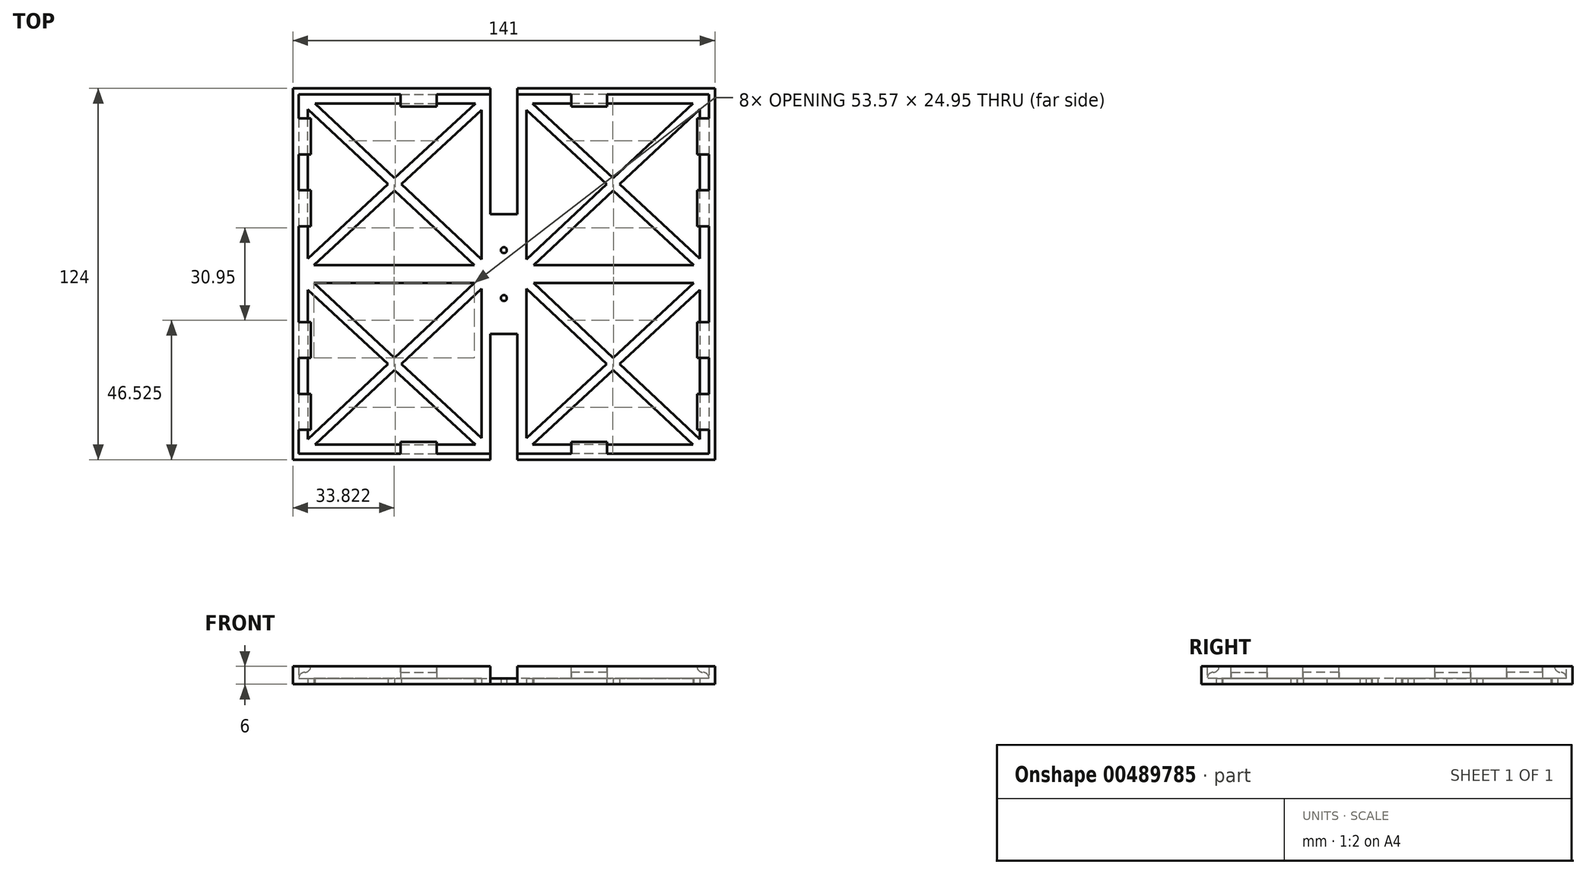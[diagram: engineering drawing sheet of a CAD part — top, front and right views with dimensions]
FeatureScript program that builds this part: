
annotation { "Feature Type Name" : "Feature", "Feature Type Description" : "" }
export const myFeature = defineFeature(function(context is Context, id is Id, definition is map)
    precondition{}
    {
        {
            var Q0;
            Q0=qCreatedBy(makeId("Top.planeOp"),FACE);
            var sketch = newSketch(context, id + "F0", { "sketchPlane" : qUnion([Q0])});
            skLineSegment(sketch, "E0.bottom", {"start": v(-68.5, 60) * mm, "end": v(-4.5, 60) * mm});
            skLineSegment(sketch, "E0.top", {"start": v(-68.5, -60) * mm, "end": v(-4.5, -60) * mm});
            skLineSegment(sketch, "E0.left", {"start": v(-68.5, 60) * mm, "end": v(-68.5, -60) * mm});
            skLineSegment(sketch, "E0.right", {"start": v(-4.5, 60) * mm, "end": v(-4.5, -60) * mm});
            skLineSegment(sketch, "E1.MirrorCS", {"start": v(68.5, 60) * mm, "end": v(4.5, 60) * mm});
            skLineSegment(sketch, "E2.MirrorCS", {"start": v(4.5, 60) * mm, "end": v(4.5, -60) * mm});
            skLineSegment(sketch, "E3.MirrorCS", {"start": v(68.5, -60) * mm, "end": v(4.5, -60) * mm});
            skLineSegment(sketch, "E4.MirrorCS", {"start": v(68.5, 60) * mm, "end": v(68.5, -60) * mm});
            skSolve(sketch);
        }
        {
            var Q0;
            Q0=qCreatedBy(makeId("Top.planeOp"),FACE);
            var sketch = newSketch(context, id + "F1", { "sketchPlane" : qUnion([Q0])});
            skLineSegment(sketch, "E5.bottom", {"start": v(-4.5, 62) * mm, "end": v(-70.5, 62) * mm});
            skLineSegment(sketch, "E5.top", {"start": v(-4.5, -62) * mm, "end": v(-70.5, -62) * mm});
            skLineSegment(sketch, "E5.left", {"start": v(-4.5, 62) * mm, "end": v(-4.5, -62) * mm});
            skLineSegment(sketch, "E5.right", {"start": v(-70.5, 62) * mm, "end": v(-70.5, -62) * mm});
            skLineSegment(sketch, "E6.bottom", {"start": v(70.5, 62) * mm, "end": v(4.5, 62) * mm});
            skLineSegment(sketch, "E6.top", {"start": v(70.5, -62) * mm, "end": v(4.5, -62) * mm});
            skLineSegment(sketch, "E6.left", {"start": v(70.5, 62) * mm, "end": v(70.5, -62) * mm});
            skLineSegment(sketch, "E6.right", {"start": v(4.5, 62) * mm, "end": v(4.5, -62) * mm});
            skLineSegment(sketch, "E7.bottom", {"start": v(-68.5, 60) * mm, "end": v(-4.5, 60) * mm});
            skLineSegment(sketch, "E7.top", {"start": v(-68.5, -60) * mm, "end": v(-4.5, -60) * mm});
            skLineSegment(sketch, "E7.left", {"start": v(-68.5, 60) * mm, "end": v(-68.5, -60) * mm});
            skLineSegment(sketch, "E7.right", {"start": v(-4.5, 60) * mm, "end": v(-4.5, -60) * mm});
            skLineSegment(sketch, "E8.bottom", {"start": v(4.5, 60) * mm, "end": v(68.5, 60) * mm});
            skLineSegment(sketch, "E8.top", {"start": v(4.5, -60) * mm, "end": v(68.5, -60) * mm});
            skLineSegment(sketch, "E8.left", {"start": v(4.5, 60) * mm, "end": v(4.5, -60) * mm});
            skLineSegment(sketch, "E8.right", {"start": v(68.5, 60) * mm, "end": v(68.5, -60) * mm});
            skSolve(sketch);
        }
        {
            var Q0;
            Q0=makeQuery(id+"F0.imprint","IMPRINT",FACE,{"disambiguationData":[TD([[makeQuery(id+"F0.imprint","IMPRINT",EDGE,{"derivedFrom":sQuery(id+"F0.wireOp",EDGE,"E0.bottom")}),-1.0]])]});
            var Q1;
            Q1=makeQuery(id+"F0.imprint","IMPRINT",FACE,{"disambiguationData":[TD([[makeQuery(id+"F0.imprint","IMPRINT",EDGE,{"derivedFrom":sQuery(id+"F0.wireOp",EDGE,"E1.MirrorCS")}),1.0]])]});
            extrude(context, id + "F2", {"entities" : qUnion([Q0, Q1]), "depth" : 2 * mm});
        }
        {
            var Q0;
            {var subQ4=sQuery(id+"F1.wireOp",EDGE,"E5.bottom");Q0=makeQuery(id+"F1.imprint","IMPRINT",FACE,{"disambiguationData":[TD([[makeQuery(id+"F1.imprint","IMPRINT",EDGE,{"derivedFrom":subQ4}),1.0]])]});}
            var Q1;
            {var subQ1=sQuery(id+"F1.wireOp",EDGE,"E6.bottom");Q1=makeQuery(id+"F1.imprint","IMPRINT",FACE,{"disambiguationData":[TD([[makeQuery(id+"F1.imprint","IMPRINT",EDGE,{"derivedFrom":subQ1}),1.0]])]});}
            extrude(context, id + "F3", {"entities" : qUnion([Q0, Q1]), "operationType" : NewBodyOperationType.ADD, "depth" : 6 * mm});
        }
        {
            var Q0;
            Q0=makeQuery(id+"F3.opExtrude","CAP_FACE",FACE,{"disambiguationData":[OSD([sQuery(id+"F1.wireOp",EDGE,"E5.bottom"),sQuery(id+"F1.wireOp",EDGE,"E5.top"),sQuery(id+"F1.wireOp",EDGE,"E5.left"),sQuery(id+"F1.wireOp",EDGE,"E5.right"),sQuery(id+"F1.wireOp",EDGE,"E7.bottom"),sQuery(id+"F1.wireOp",EDGE,"E7.top"),sQuery(id+"F1.wireOp",EDGE,"E7.left")])],"isStart":false});
            var sketch = newSketch(context, id + "F4", { "sketchPlane" : qUnion([Q0])});
            skLineSegment(sketch, "E9.bottom", {"start": v(-70.5, 52) * mm, "end": v(-64.5, 52) * mm});
            skLineSegment(sketch, "E9.top", {"start": v(-70.5, 40) * mm, "end": v(-64.5, 40) * mm});
            skLineSegment(sketch, "E9.left", {"start": v(-70.5, 52) * mm, "end": v(-70.5, 40) * mm});
            skLineSegment(sketch, "E9.right", {"start": v(-64.5, 52) * mm, "end": v(-64.5, 40) * mm});
            skLineSegment(sketch, "E10.bottom", {"start": v(-34.5, 62) * mm, "end": v(-22.5, 62) * mm});
            skLineSegment(sketch, "E10.top", {"start": v(-34.5, 56) * mm, "end": v(-22.5, 56) * mm});
            skLineSegment(sketch, "E10.left", {"start": v(-34.5, 62) * mm, "end": v(-34.5, 56) * mm});
            skLineSegment(sketch, "E10.right", {"start": v(-22.5, 62) * mm, "end": v(-22.5, 56) * mm});
            skLineSegment(sketch, "E11.bottom", {"start": v(-70.5, 16) * mm, "end": v(-64.5, 16) * mm});
            skLineSegment(sketch, "E11.top", {"start": v(-70.5, 28) * mm, "end": v(-64.5, 28) * mm});
            skLineSegment(sketch, "E11.left", {"start": v(-70.5, 16) * mm, "end": v(-70.5, 28) * mm});
            skLineSegment(sketch, "E11.right", {"start": v(-64.5, 16) * mm, "end": v(-64.5, 28) * mm});
            skLineSegment(sketch, "E12.MirrorCS", {"start": v(-22.5, -62) * mm, "end": v(-22.5, -56) * mm});
            skLineSegment(sketch, "E13.MirrorCS", {"start": v(-34.5, -62) * mm, "end": v(-34.5, -56) * mm});
            skLineSegment(sketch, "E14.MirrorCS", {"start": v(-64.5, -16) * mm, "end": v(-64.5, -28) * mm});
            skLineSegment(sketch, "E15.MirrorCS", {"start": v(-70.5, -52) * mm, "end": v(-70.5, -40) * mm});
            skLineSegment(sketch, "E16.MirrorCS", {"start": v(-70.5, -16) * mm, "end": v(-70.5, -28) * mm});
            skLineSegment(sketch, "E17.MirrorCS", {"start": v(-70.5, -28) * mm, "end": v(-64.5, -28) * mm});
            skLineSegment(sketch, "E18.MirrorCS", {"start": v(-70.5, -40) * mm, "end": v(-64.5, -40) * mm});
            skLineSegment(sketch, "E19.MirrorCS", {"start": v(-70.5, -52) * mm, "end": v(-64.5, -52) * mm});
            skLineSegment(sketch, "E20.MirrorCS", {"start": v(-70.5, -16) * mm, "end": v(-64.5, -16) * mm});
            skLineSegment(sketch, "E21.MirrorCS", {"start": v(-64.5, -52) * mm, "end": v(-64.5, -40) * mm});
            skLineSegment(sketch, "E22.MirrorCS", {"start": v(-34.5, -56) * mm, "end": v(-22.5, -56) * mm});
            skLineSegment(sketch, "E23.MirrorCS", {"start": v(-34.5, -62) * mm, "end": v(-22.5, -62) * mm});
            skLineSegment(sketch, "E24.MirrorCS", {"start": v(70.5, 40) * mm, "end": v(64.5, 40) * mm});
            skLineSegment(sketch, "E25.MirrorCS", {"start": v(70.5, -28) * mm, "end": v(64.5, -28) * mm});
            skLineSegment(sketch, "E26.MirrorCS", {"start": v(70.5, -40) * mm, "end": v(64.5, -40) * mm});
            skLineSegment(sketch, "E27.MirrorCS", {"start": v(70.5, -52) * mm, "end": v(64.5, -52) * mm});
            skLineSegment(sketch, "E28.MirrorCS", {"start": v(34.5, 62) * mm, "end": v(34.5, 56) * mm});
            skLineSegment(sketch, "E29.MirrorCS", {"start": v(22.5, 62) * mm, "end": v(22.5, 56) * mm});
            skLineSegment(sketch, "E30.MirrorCS", {"start": v(70.5, 16) * mm, "end": v(64.5, 16) * mm});
            skLineSegment(sketch, "E31.MirrorCS", {"start": v(70.5, 28) * mm, "end": v(64.5, 28) * mm});
            skLineSegment(sketch, "E32.MirrorCS", {"start": v(70.5, -16) * mm, "end": v(64.5, -16) * mm});
            skLineSegment(sketch, "E33.MirrorCS", {"start": v(70.5, 52) * mm, "end": v(64.5, 52) * mm});
            skLineSegment(sketch, "E34.MirrorCS", {"start": v(64.5, 16) * mm, "end": v(64.5, 28) * mm});
            skLineSegment(sketch, "E35.MirrorCS", {"start": v(34.5, -62) * mm, "end": v(22.5, -62) * mm});
            skLineSegment(sketch, "E36.MirrorCS", {"start": v(34.5, -56) * mm, "end": v(22.5, -56) * mm});
            skLineSegment(sketch, "E37.MirrorCS", {"start": v(70.5, 52) * mm, "end": v(70.5, 40) * mm});
            skLineSegment(sketch, "E38.MirrorCS", {"start": v(64.5, 52) * mm, "end": v(64.5, 40) * mm});
            skLineSegment(sketch, "E39.MirrorCS", {"start": v(64.5, -52) * mm, "end": v(64.5, -40) * mm});
            skLineSegment(sketch, "E40.MirrorCS", {"start": v(34.5, 62) * mm, "end": v(22.5, 62) * mm});
            skLineSegment(sketch, "E41.MirrorCS", {"start": v(34.5, 56) * mm, "end": v(22.5, 56) * mm});
            skLineSegment(sketch, "E42.MirrorCS", {"start": v(34.5, -62) * mm, "end": v(34.5, -56) * mm});
            skLineSegment(sketch, "E43.MirrorCS", {"start": v(70.5, -16) * mm, "end": v(70.5, -28) * mm});
            skLineSegment(sketch, "E44.MirrorCS", {"start": v(70.5, 16) * mm, "end": v(70.5, 28) * mm});
            skLineSegment(sketch, "E45.MirrorCS", {"start": v(70.5, -52) * mm, "end": v(70.5, -40) * mm});
            skLineSegment(sketch, "E46.MirrorCS", {"start": v(64.5, -16) * mm, "end": v(64.5, -28) * mm});
            skLineSegment(sketch, "E47.MirrorCS", {"start": v(22.5, -62) * mm, "end": v(22.5, -56) * mm});
            skSolve(sketch);
        }
        {
            var Q0;
            Q0=qSketchRegion(id+"F4",true);
            extrude(context, id + "F5", {"entities" : qUnion([Q0]), "operationType" : NewBodyOperationType.ADD, "oppositeDirection" : true, "depth" : 2 * mm});
        }
        {
            var Q0;
            Q0=makeQuery(id+"F2.opExtrude","CAP_FACE",FACE,{"disambiguationData":[OSD([sQuery(id+"F0.wireOp",EDGE,"E0.bottom"),sQuery(id+"F0.wireOp",EDGE,"E0.top"),sQuery(id+"F0.wireOp",EDGE,"E0.left"),sQuery(id+"F0.wireOp",EDGE,"E0.right")])],"isStart":true});
            var sketch = newSketch(context, id + "F6", { "sketchPlane" : qUnion([Q0])});
            skLineSegment(sketch, "E48", {"start": v(-63.1, 57) * mm, "end": v(-7.5, 57) * mm});
            skLineSegment(sketch, "E49", {"start": v(-7.5, 57) * mm, "end": v(-7.5, 4.87) * mm});
            skLineSegment(sketch, "E50", {"start": v(-7.5, 4.87) * mm, "end": v(-63.1, 57) * mm});
            skLineSegment(sketch, "E51", {"start": v(-65.5, 55.13) * mm, "end": v(-9.9, 3) * mm});
            skLineSegment(sketch, "E52", {"start": v(-9.9, 3) * mm, "end": v(-65.5, 3) * mm});
            skLineSegment(sketch, "E53", {"start": v(-65.5, 3) * mm, "end": v(-65.5, 55.13) * mm});
            skLineSegment(sketch, "E54", {"start": v(-9.54, 57) * mm, "end": v(-65.5, 5.2) * mm});
            skLineSegment(sketch, "E55", {"start": v(-65.5, 5.2) * mm, "end": v(-63.46, 3) * mm});
            skLineSegment(sketch, "E56", {"start": v(-63.46, 3) * mm, "end": v(-7.5, 54.8) * mm});
            skLineSegment(sketch, "E57", {"start": v(-7.5, 54.8) * mm, "end": v(-9.54, 57) * mm});
            skLineSegment(sketch, "E58", {"start": v(-68.5, 60) * mm, "end": v(-4.5, 0) * mm});
            skLineSegment(sketch, "E59.MirrorCS", {"start": v(-7.5, -54.8) * mm, "end": v(-9.54, -57) * mm});
            skLineSegment(sketch, "E60.MirrorCS", {"start": v(-65.5, -5.2) * mm, "end": v(-63.46, -3) * mm});
            skLineSegment(sketch, "E61.MirrorCS", {"start": v(-63.1, -57) * mm, "end": v(-7.5, -57) * mm});
            skLineSegment(sketch, "E62.MirrorCS", {"start": v(-7.5, -57) * mm, "end": v(-7.5, -4.87) * mm});
            skLineSegment(sketch, "E63.MirrorCS", {"start": v(-7.5, -4.87) * mm, "end": v(-63.1, -57) * mm});
            skLineSegment(sketch, "E64.MirrorCS", {"start": v(-65.5, -55.13) * mm, "end": v(-9.9, -3) * mm});
            skLineSegment(sketch, "E65.MirrorCS", {"start": v(-63.46, -3) * mm, "end": v(-7.5, -54.8) * mm});
            skLineSegment(sketch, "E66.MirrorCS", {"start": v(-9.9, -3) * mm, "end": v(-65.5, -3) * mm});
            skLineSegment(sketch, "E67.MirrorCS", {"start": v(-68.5, -60) * mm, "end": v(-4.5, 0) * mm});
            skLineSegment(sketch, "E68.MirrorCS", {"start": v(-9.54, -57) * mm, "end": v(-65.5, -5.2) * mm});
            skLineSegment(sketch, "E69.MirrorCS", {"start": v(-65.5, -3) * mm, "end": v(-65.5, -55.13) * mm});
            skLineSegment(sketch, "E70.MirrorCS", {"start": v(65.5, -5.2) * mm, "end": v(63.46, -3) * mm});
            skLineSegment(sketch, "E71.MirrorCS", {"start": v(7.5, 54.8) * mm, "end": v(9.54, 57) * mm});
            skLineSegment(sketch, "E72.MirrorCS", {"start": v(7.5, -54.8) * mm, "end": v(9.54, -57) * mm});
            skLineSegment(sketch, "E73.MirrorCS", {"start": v(65.5, 5.2) * mm, "end": v(63.46, 3) * mm});
            skLineSegment(sketch, "E74.MirrorCS", {"start": v(9.9, -3) * mm, "end": v(65.5, -3) * mm});
            skLineSegment(sketch, "E75.MirrorCS", {"start": v(63.46, 3) * mm, "end": v(7.5, 54.8) * mm});
            skLineSegment(sketch, "E76.MirrorCS", {"start": v(9.54, 57) * mm, "end": v(65.5, 5.2) * mm});
            skLineSegment(sketch, "E77.MirrorCS", {"start": v(9.9, 3) * mm, "end": v(65.5, 3) * mm});
            skLineSegment(sketch, "E78.MirrorCS", {"start": v(68.5, 60) * mm, "end": v(4.5, 0) * mm});
            skLineSegment(sketch, "E79.MirrorCS", {"start": v(65.5, 55.13) * mm, "end": v(9.9, 3) * mm});
            skLineSegment(sketch, "E80.MirrorCS", {"start": v(7.5, 4.87) * mm, "end": v(63.1, 57) * mm});
            skLineSegment(sketch, "E81.MirrorCS", {"start": v(65.5, 3) * mm, "end": v(65.5, 55.13) * mm});
            skLineSegment(sketch, "E82.MirrorCS", {"start": v(7.5, -4.87) * mm, "end": v(63.1, -57) * mm});
            skLineSegment(sketch, "E83.MirrorCS", {"start": v(7.5, -57) * mm, "end": v(7.5, -4.87) * mm});
            skLineSegment(sketch, "E84.MirrorCS", {"start": v(68.5, -60) * mm, "end": v(4.5, 0) * mm});
            skLineSegment(sketch, "E85.MirrorCS", {"start": v(63.1, 57) * mm, "end": v(7.5, 57) * mm});
            skLineSegment(sketch, "E86.MirrorCS", {"start": v(65.5, -55.13) * mm, "end": v(9.9, -3) * mm});
            skLineSegment(sketch, "E87.MirrorCS", {"start": v(7.5, 57) * mm, "end": v(7.5, 4.87) * mm});
            skLineSegment(sketch, "E88.MirrorCS", {"start": v(63.1, -57) * mm, "end": v(7.5, -57) * mm});
            skLineSegment(sketch, "E89.MirrorCS", {"start": v(9.54, -57) * mm, "end": v(65.5, -5.2) * mm});
            skLineSegment(sketch, "E90.MirrorCS", {"start": v(63.46, -3) * mm, "end": v(7.5, -54.8) * mm});
            skLineSegment(sketch, "E91.MirrorCS", {"start": v(65.5, -3) * mm, "end": v(65.5, -55.13) * mm});
            skSolve(sketch);
        }
        {
            var Q0;
            {var subQ0=sQuery(id+"F6.wireOp",EDGE,"E50");var subQ1=sQuery(id+"F6.wireOp",EDGE,"E48");var subQ2=makeQuery(id+"F6.imprint","INTERSECT",VERTEX,{"derivedFrom":[subQ1,subQ0]});Q0=makeQuery(id+"F6.imprint","IMPRINT",FACE,{"disambiguationData":[TD([[makeQuery(id+"F6.imprint","IMPRINT",EDGE,{"disambiguationData":[TD([[subQ2,1.0]])],"derivedFrom":subQ0}),-1.0]])]});}
            var Q1;
            {var subQ0=sQuery(id+"F6.wireOp",EDGE,"E50");var subQ1=sQuery(id+"F6.wireOp",EDGE,"E49");var subQ2=makeQuery(id+"F6.imprint","INTERSECT",VERTEX,{"derivedFrom":[subQ1,subQ0]});Q1=makeQuery(id+"F6.imprint","IMPRINT",FACE,{"disambiguationData":[TD([[makeQuery(id+"F6.imprint","IMPRINT",EDGE,{"disambiguationData":[TD([[subQ2,-1.0]])],"derivedFrom":subQ0}),-1.0]])]});}
            var Q2;
            {var subQ0=sQuery(id+"F6.wireOp",EDGE,"E52");var subQ1=sQuery(id+"F6.wireOp",EDGE,"E51");var subQ2=makeQuery(id+"F6.imprint","INTERSECT",VERTEX,{"derivedFrom":[subQ1,subQ0]});Q2=makeQuery(id+"F6.imprint","IMPRINT",FACE,{"disambiguationData":[TD([[makeQuery(id+"F6.imprint","IMPRINT",EDGE,{"disambiguationData":[TD([[subQ2,1.0]])],"derivedFrom":subQ1}),-1.0]])]});}
            var Q3;
            {var subQ0=sQuery(id+"F6.wireOp",EDGE,"E53");var subQ1=sQuery(id+"F6.wireOp",EDGE,"E51");var subQ2=makeQuery(id+"F6.imprint","INTERSECT",VERTEX,{"derivedFrom":[subQ1,subQ0]});Q3=makeQuery(id+"F6.imprint","IMPRINT",FACE,{"disambiguationData":[TD([[makeQuery(id+"F6.imprint","IMPRINT",EDGE,{"disambiguationData":[TD([[subQ2,-1.0]])],"derivedFrom":subQ1}),-1.0]])]});}
            var Q4;
            {var subQ0=sQuery(id+"F6.wireOp",EDGE,"E66.MirrorCS");var subQ1=sQuery(id+"F6.wireOp",EDGE,"E64.MirrorCS");var subQ2=makeQuery(id+"F6.imprint","INTERSECT",VERTEX,{"derivedFrom":[subQ1,subQ0]});Q4=makeQuery(id+"F6.imprint","IMPRINT",FACE,{"disambiguationData":[TD([[makeQuery(id+"F6.imprint","IMPRINT",EDGE,{"disambiguationData":[TD([[subQ2,1.0]])],"derivedFrom":subQ1}),1.0]])]});}
            var Q5;
            {var subQ1=sQuery(id+"F6.wireOp",EDGE,"E62.MirrorCS");var subQ3=sQuery(id+"F6.wireOp",EDGE,"E63.MirrorCS");var subQ4=makeQuery(id+"F6.imprint","INTERSECT",VERTEX,{"derivedFrom":[subQ1,subQ3]});Q5=makeQuery(id+"F6.imprint","IMPRINT",FACE,{"disambiguationData":[TD([[makeQuery(id+"F6.imprint","IMPRINT",EDGE,{"disambiguationData":[TD([[subQ4,-1.0]])],"derivedFrom":subQ3}),1.0]])]});}
            var Q6;
            {var subQ1=sQuery(id+"F6.wireOp",EDGE,"E61.MirrorCS");var subQ3=sQuery(id+"F6.wireOp",EDGE,"E63.MirrorCS");var subQ4=makeQuery(id+"F6.imprint","INTERSECT",VERTEX,{"derivedFrom":[subQ1,subQ3]});Q6=makeQuery(id+"F6.imprint","IMPRINT",FACE,{"disambiguationData":[TD([[makeQuery(id+"F6.imprint","IMPRINT",EDGE,{"disambiguationData":[TD([[subQ4,1.0]])],"derivedFrom":subQ3}),1.0]])]});}
            var Q7;
            {var subQ0=sQuery(id+"F6.wireOp",EDGE,"E69.MirrorCS");var subQ1=sQuery(id+"F6.wireOp",EDGE,"E64.MirrorCS");var subQ2=makeQuery(id+"F6.imprint","INTERSECT",VERTEX,{"derivedFrom":[subQ1,subQ0]});Q7=makeQuery(id+"F6.imprint","IMPRINT",FACE,{"disambiguationData":[TD([[makeQuery(id+"F6.imprint","IMPRINT",EDGE,{"disambiguationData":[TD([[subQ2,-1.0]])],"derivedFrom":subQ1}),1.0]])]});}
            var Q8;
            {var subQ0=sQuery(id+"F6.wireOp",EDGE,"E83.MirrorCS");var subQ1=sQuery(id+"F6.wireOp",EDGE,"E82.MirrorCS");var subQ2=makeQuery(id+"F6.imprint","INTERSECT",VERTEX,{"derivedFrom":[subQ1,subQ0]});Q8=makeQuery(id+"F6.imprint","IMPRINT",FACE,{"disambiguationData":[TD([[makeQuery(id+"F6.imprint","IMPRINT",EDGE,{"disambiguationData":[TD([[subQ2,-1.0]])],"derivedFrom":subQ1}),-1.0]])]});}
            var Q9;
            {var subQ0=sQuery(id+"F6.wireOp",EDGE,"E88.MirrorCS");var subQ1=sQuery(id+"F6.wireOp",EDGE,"E82.MirrorCS");var subQ2=makeQuery(id+"F6.imprint","INTERSECT",VERTEX,{"derivedFrom":[subQ1,subQ0]});Q9=makeQuery(id+"F6.imprint","IMPRINT",FACE,{"disambiguationData":[TD([[makeQuery(id+"F6.imprint","IMPRINT",EDGE,{"disambiguationData":[TD([[subQ2,1.0]])],"derivedFrom":subQ1}),-1.0]])]});}
            var Q10;
            {var subQ0=sQuery(id+"F6.wireOp",EDGE,"E91.MirrorCS");var subQ1=sQuery(id+"F6.wireOp",EDGE,"E86.MirrorCS");var subQ2=makeQuery(id+"F6.imprint","INTERSECT",VERTEX,{"derivedFrom":[subQ1,subQ0]});Q10=makeQuery(id+"F6.imprint","IMPRINT",FACE,{"disambiguationData":[TD([[makeQuery(id+"F6.imprint","IMPRINT",EDGE,{"disambiguationData":[TD([[subQ2,-1.0]])],"derivedFrom":subQ1}),-1.0]])]});}
            var Q11;
            {var subQ1=sQuery(id+"F6.wireOp",EDGE,"E74.MirrorCS");var subQ3=sQuery(id+"F6.wireOp",EDGE,"E86.MirrorCS");var subQ4=makeQuery(id+"F6.imprint","INTERSECT",VERTEX,{"derivedFrom":[subQ1,subQ3]});Q11=makeQuery(id+"F6.imprint","IMPRINT",FACE,{"disambiguationData":[TD([[makeQuery(id+"F6.imprint","IMPRINT",EDGE,{"disambiguationData":[TD([[subQ4,1.0]])],"derivedFrom":subQ3}),-1.0]])]});}
            var Q12;
            {var subQ0=sQuery(id+"F6.wireOp",EDGE,"E77.MirrorCS");var subQ3=sQuery(id+"F6.wireOp",EDGE,"E79.MirrorCS");var subQ5=makeQuery(id+"F6.imprint","INTERSECT",VERTEX,{"derivedFrom":[subQ0,subQ3]});Q12=makeQuery(id+"F6.imprint","IMPRINT",FACE,{"disambiguationData":[TD([[makeQuery(id+"F6.imprint","IMPRINT",EDGE,{"disambiguationData":[TD([[subQ5,1.0]])],"derivedFrom":subQ3}),1.0]])]});}
            var Q13;
            {var subQ0=sQuery(id+"F6.wireOp",EDGE,"E87.MirrorCS");var subQ3=sQuery(id+"F6.wireOp",EDGE,"E80.MirrorCS");var subQ5=makeQuery(id+"F6.imprint","INTERSECT",VERTEX,{"derivedFrom":[subQ3,subQ0]});Q13=makeQuery(id+"F6.imprint","IMPRINT",FACE,{"disambiguationData":[TD([[makeQuery(id+"F6.imprint","IMPRINT",EDGE,{"disambiguationData":[TD([[subQ5,-1.0]])],"derivedFrom":subQ3}),1.0]])]});}
            var Q14;
            {var subQ0=sQuery(id+"F6.wireOp",EDGE,"E85.MirrorCS");var subQ3=sQuery(id+"F6.wireOp",EDGE,"E80.MirrorCS");var subQ5=makeQuery(id+"F6.imprint","INTERSECT",VERTEX,{"derivedFrom":[subQ3,subQ0]});Q14=makeQuery(id+"F6.imprint","IMPRINT",FACE,{"disambiguationData":[TD([[makeQuery(id+"F6.imprint","IMPRINT",EDGE,{"disambiguationData":[TD([[subQ5,1.0]])],"derivedFrom":subQ3}),1.0]])]});}
            var Q15;
            {var subQ0=sQuery(id+"F6.wireOp",EDGE,"E81.MirrorCS");var subQ3=sQuery(id+"F6.wireOp",EDGE,"E79.MirrorCS");var subQ5=makeQuery(id+"F6.imprint","INTERSECT",VERTEX,{"derivedFrom":[subQ3,subQ0]});Q15=makeQuery(id+"F6.imprint","IMPRINT",FACE,{"disambiguationData":[TD([[makeQuery(id+"F6.imprint","IMPRINT",EDGE,{"disambiguationData":[TD([[subQ5,-1.0]])],"derivedFrom":subQ3}),1.0]])]});}
            extrude(context, id + "F7", {"entities" : qUnion([Q0, Q1, Q2, Q3, Q4, Q5, Q6, Q7, Q8, Q9, Q10, Q11, Q12, Q13, Q14, Q15]), "operationType" : NewBodyOperationType.REMOVE, "oppositeDirection" : true, "depth" : 2 * mm});
        }
        {
            var Q0;
            Q0=makeQuery(id+"F3.boolean.opBoolean","MERGE",FACE,{"derivedFrom":[makeQuery(id+"F2.opExtrude","CAP_FACE",FACE,{"disambiguationData":[OSD([sQuery(id+"F0.wireOp",EDGE,"E1.MirrorCS"),sQuery(id+"F0.wireOp",EDGE,"E2.MirrorCS"),sQuery(id+"F0.wireOp",EDGE,"E3.MirrorCS"),sQuery(id+"F0.wireOp",EDGE,"E4.MirrorCS")])],"isStart":true}),makeQuery(id+"F3.opExtrude","CAP_FACE",FACE,{"disambiguationData":[OSD([sQuery(id+"F1.wireOp",EDGE,"E6.bottom"),sQuery(id+"F1.wireOp",EDGE,"E6.top"),sQuery(id+"F1.wireOp",EDGE,"E6.left"),sQuery(id+"F1.wireOp",EDGE,"E6.right"),sQuery(id+"F1.wireOp",EDGE,"E8.bottom"),sQuery(id+"F1.wireOp",EDGE,"E8.top"),sQuery(id+"F1.wireOp",EDGE,"E8.right")])],"isStart":true})]});
            var sketch = newSketch(context, id + "F8", { "sketchPlane" : qUnion([Q0])});
            skLineSegment(sketch, "E92.bottom", {"start": v(-4.5, 20) * mm, "end": v(4.5, 20) * mm});
            skLineSegment(sketch, "E92.top", {"start": v(-4.5, -20) * mm, "end": v(4.5, -20) * mm});
            skLineSegment(sketch, "E92.left", {"start": v(-4.5, 20) * mm, "end": v(-4.5, -20) * mm});
            skLineSegment(sketch, "E92.right", {"start": v(4.5, 20) * mm, "end": v(4.5, -20) * mm});
            skCircle(sketch, "E93", {"center": v(0, 8) * mm, "radius": 1 * mm});
            skCircle(sketch, "E94", {"center": v(0, -8) * mm, "radius": 1 * mm});
            skSolve(sketch);
        }
        {
            var Q0;
            Q0=makeQuery(id+"F8.imprint","IMPRINT",FACE,{"disambiguationData":[TD([[makeQuery(id+"F8.imprint","IMPRINT",EDGE,{"derivedFrom":sQuery(id+"F8.wireOp",EDGE,"E92.bottom")}),-1.0]])]});
            extrude(context, id + "F9", {"entities" : qUnion([Q0]), "operationType" : NewBodyOperationType.ADD, "oppositeDirection" : true, "depth" : 2 * mm});
        }
        {
            var Q0;
            Q0=makeQuery(id+"F5.opExtrude","CAP_EDGE",EDGE,{"disambiguationData":[OSD([sQuery(id+"F4.wireOp",EDGE,"E36.MirrorCS")])],"isStart":false});
            var Q1;
            Q1=makeQuery(id+"F5.opExtrude","CAP_EDGE",EDGE,{"disambiguationData":[OSD([sQuery(id+"F4.wireOp",EDGE,"E22.MirrorCS")])],"isStart":false});
            var Q2;
            Q2=makeQuery(id+"F5.opExtrude","CAP_EDGE",EDGE,{"disambiguationData":[OSD([sQuery(id+"F4.wireOp",EDGE,"E39.MirrorCS")])],"isStart":false});
            var Q3;
            Q3=makeQuery(id+"F5.opExtrude","CAP_EDGE",EDGE,{"disambiguationData":[OSD([sQuery(id+"F4.wireOp",EDGE,"E46.MirrorCS")])],"isStart":false});
            var Q4;
            Q4=makeQuery(id+"F5.opExtrude","CAP_EDGE",EDGE,{"disambiguationData":[OSD([sQuery(id+"F4.wireOp",EDGE,"E21.MirrorCS")])],"isStart":false});
            var Q5;
            Q5=makeQuery(id+"F5.opExtrude","CAP_EDGE",EDGE,{"disambiguationData":[OSD([sQuery(id+"F4.wireOp",EDGE,"E14.MirrorCS")])],"isStart":false});
            var Q6;
            Q6=makeQuery(id+"F5.opExtrude","CAP_EDGE",EDGE,{"disambiguationData":[OSD([sQuery(id+"F4.wireOp",EDGE,"E34.MirrorCS")])],"isStart":false});
            var Q7;
            Q7=makeQuery(id+"F5.opExtrude","CAP_EDGE",EDGE,{"disambiguationData":[OSD([sQuery(id+"F4.wireOp",EDGE,"E38.MirrorCS")])],"isStart":false});
            var Q8;
            Q8=makeQuery(id+"F5.opExtrude","CAP_EDGE",EDGE,{"disambiguationData":[OSD([sQuery(id+"F4.wireOp",EDGE,"E10.top")])],"isStart":false});
            var Q9;
            Q9=makeQuery(id+"F5.opExtrude","CAP_EDGE",EDGE,{"disambiguationData":[OSD([sQuery(id+"F4.wireOp",EDGE,"E41.MirrorCS")])],"isStart":false});
            var Q10;
            Q10=makeQuery(id+"F5.opExtrude","CAP_EDGE",EDGE,{"disambiguationData":[OSD([sQuery(id+"F4.wireOp",EDGE,"E11.right")])],"isStart":false});
            var Q11;
            Q11=makeQuery(id+"F5.opExtrude","CAP_EDGE",EDGE,{"disambiguationData":[OSD([sQuery(id+"F4.wireOp",EDGE,"E9.right")])],"isStart":false});
            fillet(context, id + "F10", {"entities" : qUnion([Q0, Q1, Q2, Q3, Q4, Q5, Q6, Q7, Q8, Q9, Q10, Q11]), "radius" : 2 * mm, "tangentPropagation" : true, "allowEdgeOverflow" : false});
        }
        {
            var Q0;
            Q0=makeQuery(id+"F5.boolean.opBoolean","INTERSECT",EDGE,{"derivedFrom":[makeQuery(id+"F3.opExtrude","SWEPT_FACE",FACE,{"disambiguationData":[OSD([sQuery(id+"F1.wireOp",EDGE,"E8.top")])]}),makeQuery(id+"F5.opExtrude","CAP_FACE",FACE,{"disambiguationData":[OSD([sQuery(id+"F4.wireOp",EDGE,"E35.MirrorCS"),sQuery(id+"F4.wireOp",EDGE,"E36.MirrorCS"),sQuery(id+"F4.wireOp",EDGE,"E42.MirrorCS"),sQuery(id+"F4.wireOp",EDGE,"E47.MirrorCS")])],"isStart":false})]});
            var Q1;
            Q1=makeQuery(id+"F5.boolean.opBoolean","INTERSECT",EDGE,{"derivedFrom":[makeQuery(id+"F3.opExtrude","SWEPT_FACE",FACE,{"disambiguationData":[OSD([sQuery(id+"F1.wireOp",EDGE,"E7.top")])]}),makeQuery(id+"F5.opExtrude","CAP_FACE",FACE,{"disambiguationData":[OSD([sQuery(id+"F4.wireOp",EDGE,"E12.MirrorCS"),sQuery(id+"F4.wireOp",EDGE,"E13.MirrorCS"),sQuery(id+"F4.wireOp",EDGE,"E22.MirrorCS"),sQuery(id+"F4.wireOp",EDGE,"E23.MirrorCS")])],"isStart":false})]});
            var Q2;
            Q2=makeQuery(id+"F5.boolean.opBoolean","INTERSECT",EDGE,{"derivedFrom":[makeQuery(id+"F3.opExtrude","SWEPT_FACE",FACE,{"disambiguationData":[OSD([sQuery(id+"F1.wireOp",EDGE,"E7.left")])]}),makeQuery(id+"F5.opExtrude","CAP_FACE",FACE,{"disambiguationData":[OSD([sQuery(id+"F4.wireOp",EDGE,"E15.MirrorCS"),sQuery(id+"F4.wireOp",EDGE,"E18.MirrorCS"),sQuery(id+"F4.wireOp",EDGE,"E19.MirrorCS"),sQuery(id+"F4.wireOp",EDGE,"E21.MirrorCS")])],"isStart":false})]});
            var Q3;
            Q3=makeQuery(id+"F5.boolean.opBoolean","INTERSECT",EDGE,{"derivedFrom":[makeQuery(id+"F3.opExtrude","SWEPT_FACE",FACE,{"disambiguationData":[OSD([sQuery(id+"F1.wireOp",EDGE,"E7.left")])]}),makeQuery(id+"F5.opExtrude","CAP_FACE",FACE,{"disambiguationData":[OSD([sQuery(id+"F4.wireOp",EDGE,"E14.MirrorCS"),sQuery(id+"F4.wireOp",EDGE,"E16.MirrorCS"),sQuery(id+"F4.wireOp",EDGE,"E17.MirrorCS"),sQuery(id+"F4.wireOp",EDGE,"E20.MirrorCS")])],"isStart":false})]});
            var Q4;
            Q4=makeQuery(id+"F5.boolean.opBoolean","INTERSECT",EDGE,{"derivedFrom":[makeQuery(id+"F3.opExtrude","SWEPT_FACE",FACE,{"disambiguationData":[OSD([sQuery(id+"F1.wireOp",EDGE,"E8.right")])]}),makeQuery(id+"F5.opExtrude","CAP_FACE",FACE,{"disambiguationData":[OSD([sQuery(id+"F4.wireOp",EDGE,"E26.MirrorCS"),sQuery(id+"F4.wireOp",EDGE,"E27.MirrorCS"),sQuery(id+"F4.wireOp",EDGE,"E39.MirrorCS"),sQuery(id+"F4.wireOp",EDGE,"E45.MirrorCS")])],"isStart":false})]});
            var Q5;
            Q5=makeQuery(id+"F5.boolean.opBoolean","INTERSECT",EDGE,{"derivedFrom":[makeQuery(id+"F3.opExtrude","SWEPT_FACE",FACE,{"disambiguationData":[OSD([sQuery(id+"F1.wireOp",EDGE,"E8.right")])]}),makeQuery(id+"F5.opExtrude","CAP_FACE",FACE,{"disambiguationData":[OSD([sQuery(id+"F4.wireOp",EDGE,"E25.MirrorCS"),sQuery(id+"F4.wireOp",EDGE,"E32.MirrorCS"),sQuery(id+"F4.wireOp",EDGE,"E43.MirrorCS"),sQuery(id+"F4.wireOp",EDGE,"E46.MirrorCS")])],"isStart":false})]});
            var Q6;
            Q6=makeQuery(id+"F5.boolean.opBoolean","INTERSECT",EDGE,{"derivedFrom":[makeQuery(id+"F3.opExtrude","SWEPT_FACE",FACE,{"disambiguationData":[OSD([sQuery(id+"F1.wireOp",EDGE,"E8.right")])]}),makeQuery(id+"F5.opExtrude","CAP_FACE",FACE,{"disambiguationData":[OSD([sQuery(id+"F4.wireOp",EDGE,"E24.MirrorCS"),sQuery(id+"F4.wireOp",EDGE,"E33.MirrorCS"),sQuery(id+"F4.wireOp",EDGE,"E37.MirrorCS"),sQuery(id+"F4.wireOp",EDGE,"E38.MirrorCS")])],"isStart":false})]});
            var Q7;
            Q7=makeQuery(id+"F5.boolean.opBoolean","INTERSECT",EDGE,{"derivedFrom":[makeQuery(id+"F3.opExtrude","SWEPT_FACE",FACE,{"disambiguationData":[OSD([sQuery(id+"F1.wireOp",EDGE,"E8.right")])]}),makeQuery(id+"F5.opExtrude","CAP_FACE",FACE,{"disambiguationData":[OSD([sQuery(id+"F4.wireOp",EDGE,"E30.MirrorCS"),sQuery(id+"F4.wireOp",EDGE,"E31.MirrorCS"),sQuery(id+"F4.wireOp",EDGE,"E34.MirrorCS"),sQuery(id+"F4.wireOp",EDGE,"E44.MirrorCS")])],"isStart":false})]});
            var Q8;
            Q8=makeQuery(id+"F5.boolean.opBoolean","INTERSECT",EDGE,{"derivedFrom":[makeQuery(id+"F3.opExtrude","SWEPT_FACE",FACE,{"disambiguationData":[OSD([sQuery(id+"F1.wireOp",EDGE,"E8.bottom")])]}),makeQuery(id+"F5.opExtrude","CAP_FACE",FACE,{"disambiguationData":[OSD([sQuery(id+"F4.wireOp",EDGE,"E28.MirrorCS"),sQuery(id+"F4.wireOp",EDGE,"E29.MirrorCS"),sQuery(id+"F4.wireOp",EDGE,"E40.MirrorCS"),sQuery(id+"F4.wireOp",EDGE,"E41.MirrorCS")])],"isStart":false})]});
            var Q9;
            Q9=makeQuery(id+"F5.boolean.opBoolean","INTERSECT",EDGE,{"derivedFrom":[makeQuery(id+"F3.opExtrude","SWEPT_FACE",FACE,{"disambiguationData":[OSD([sQuery(id+"F1.wireOp",EDGE,"E7.bottom")])]}),makeQuery(id+"F5.opExtrude","CAP_FACE",FACE,{"disambiguationData":[OSD([sQuery(id+"F4.wireOp",EDGE,"E10.bottom"),sQuery(id+"F4.wireOp",EDGE,"E10.top"),sQuery(id+"F4.wireOp",EDGE,"E10.left"),sQuery(id+"F4.wireOp",EDGE,"E10.right")])],"isStart":false})]});
            var Q10;
            Q10=makeQuery(id+"F5.boolean.opBoolean","INTERSECT",EDGE,{"derivedFrom":[makeQuery(id+"F3.opExtrude","SWEPT_FACE",FACE,{"disambiguationData":[OSD([sQuery(id+"F1.wireOp",EDGE,"E7.left")])]}),makeQuery(id+"F5.opExtrude","CAP_FACE",FACE,{"disambiguationData":[OSD([sQuery(id+"F4.wireOp",EDGE,"E11.bottom"),sQuery(id+"F4.wireOp",EDGE,"E11.top"),sQuery(id+"F4.wireOp",EDGE,"E11.left"),sQuery(id+"F4.wireOp",EDGE,"E11.right")])],"isStart":false})]});
            var Q11;
            Q11=makeQuery(id+"F5.boolean.opBoolean","INTERSECT",EDGE,{"derivedFrom":[makeQuery(id+"F3.opExtrude","SWEPT_FACE",FACE,{"disambiguationData":[OSD([sQuery(id+"F1.wireOp",EDGE,"E7.left")])]}),makeQuery(id+"F5.opExtrude","CAP_FACE",FACE,{"disambiguationData":[OSD([sQuery(id+"F4.wireOp",EDGE,"E9.bottom"),sQuery(id+"F4.wireOp",EDGE,"E9.top"),sQuery(id+"F4.wireOp",EDGE,"E9.left"),sQuery(id+"F4.wireOp",EDGE,"E9.right")])],"isStart":false})]});
            fillet(context, id + "F11", {"entities" : qUnion([Q0, Q1, Q2, Q3, Q4, Q5, Q6, Q7, Q8, Q9, Q10, Q11]), "radius" : 2 * mm, "tangentPropagation" : true, "allowEdgeOverflow" : false});
        }
    });
